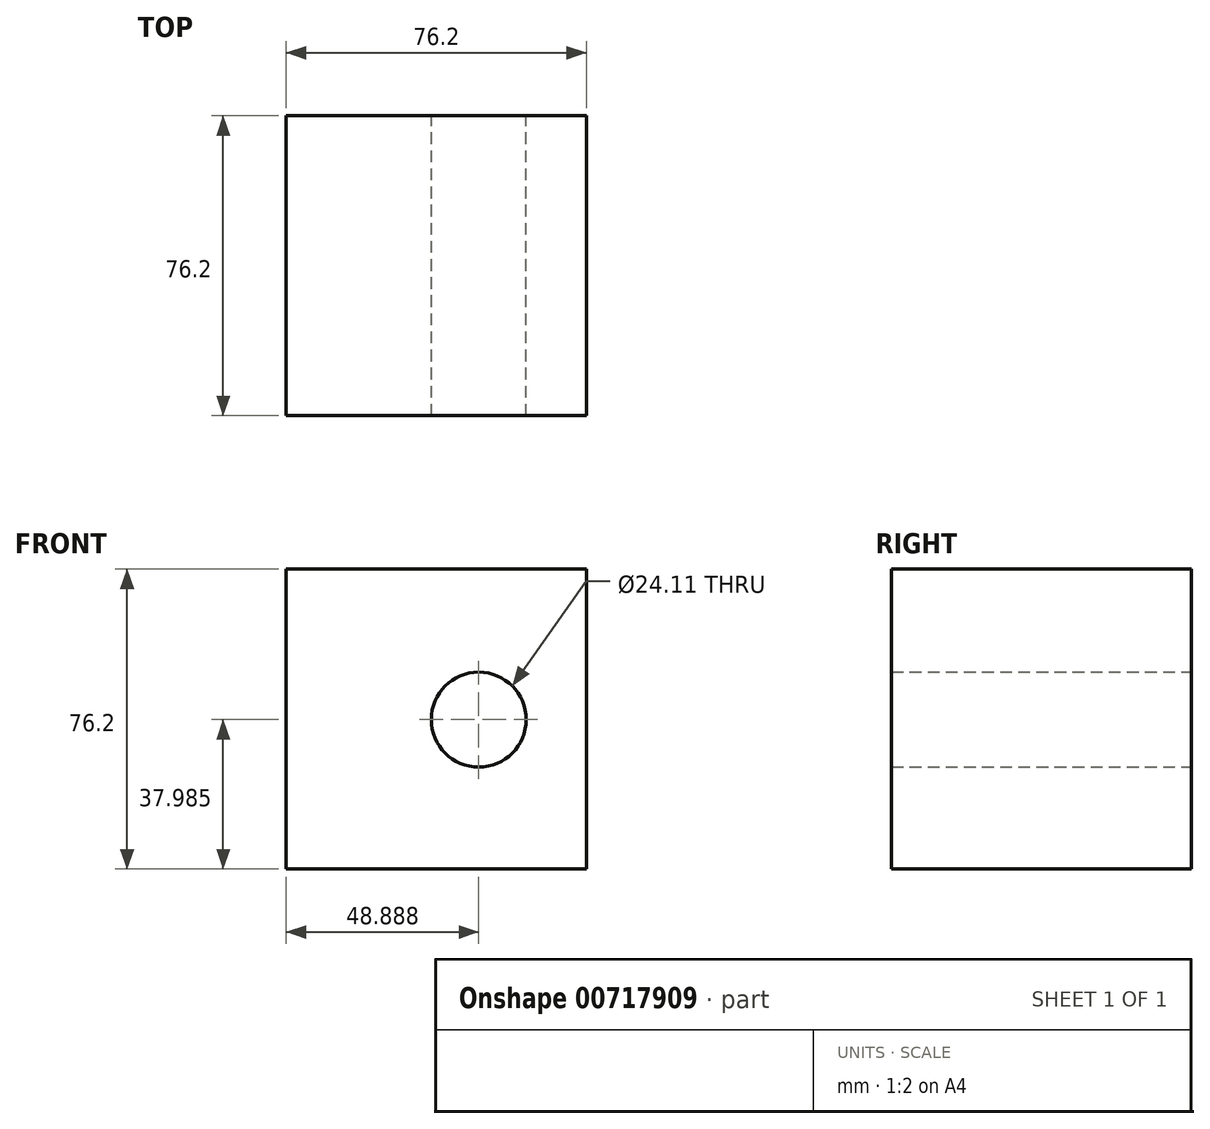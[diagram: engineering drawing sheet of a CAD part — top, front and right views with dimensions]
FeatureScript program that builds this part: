
annotation { "Feature Type Name" : "Feature", "Feature Type Description" : "" }
export const myFeature = defineFeature(function(context is Context, id is Id, definition is map)
    precondition{}
    {
        {
            var Q0;
            Q0=qCreatedBy(makeId("Front.planeOp"),FACE);
            var sketch = newSketch(context, id + "F0", { "sketchPlane" : qUnion([Q0])});
            skLineSegment(sketch, "E0.bottom", {"start": v(13.72, 24.86) * mm, "end": v(-62.48, 24.86) * mm});
            skLineSegment(sketch, "E0.top", {"start": v(13.72, -51.34) * mm, "end": v(-62.48, -51.34) * mm});
            skLineSegment(sketch, "E0.left", {"start": v(13.72, 24.86) * mm, "end": v(13.72, -51.34) * mm});
            skLineSegment(sketch, "E0.right", {"start": v(-62.48, 24.86) * mm, "end": v(-62.48, -51.34) * mm});
            skSolve(sketch);
        }
        {
            var Q0;
            Q0=makeQuery(id+"F0.imprint","IMPRINT",FACE,{"disambiguationData":[TD([[makeQuery(id+"F0.imprint","IMPRINT",EDGE,{"derivedFrom":sQuery(id+"F0.wireOp",EDGE,"E0.bottom")}),1.0]])]});
            extrude(context, id + "F1", {"entities" : qUnion([Q0]), "depth" : 76.2 * mm, "offsetDistance" : 25.4 * mm});
        }
        {
            var Q0;
            Q0=makeQuery(id+"F1.opExtrude","CAP_FACE",FACE,{"disambiguationData":[OSD([sQuery(id+"F0.wireOp",EDGE,"E0.bottom"),sQuery(id+"F0.wireOp",EDGE,"E0.top"),sQuery(id+"F0.wireOp",EDGE,"E0.left"),sQuery(id+"F0.wireOp",EDGE,"E0.right")])],"isStart":true});
            var sketch = newSketch(context, id + "F2", { "sketchPlane" : qUnion([Q0])});
            skCircle(sketch, "E1", {"center": v(13.6, -13.35) * mm, "radius": 12.06 * mm});
            skSolve(sketch);
        }
        {
            var Q0;
            Q0=makeQuery(id+"F2.imprint","IMPRINT",FACE,{"disambiguationData":[TD([[makeQuery(id+"F2.imprint","IMPRINT",EDGE,{"derivedFrom":sQuery(id+"F2.wireOp",EDGE,"E1")}),1.0]])]});
            extrude(context, id + "F3", {"entities" : qUnion([Q0]), "operationType" : NewBodyOperationType.REMOVE, "endBound" : BoundingType.THROUGH_ALL, "oppositeDirection" : true, "depth" : 101.6 * mm, "offsetDistance" : 25.4 * mm});
        }
    });
